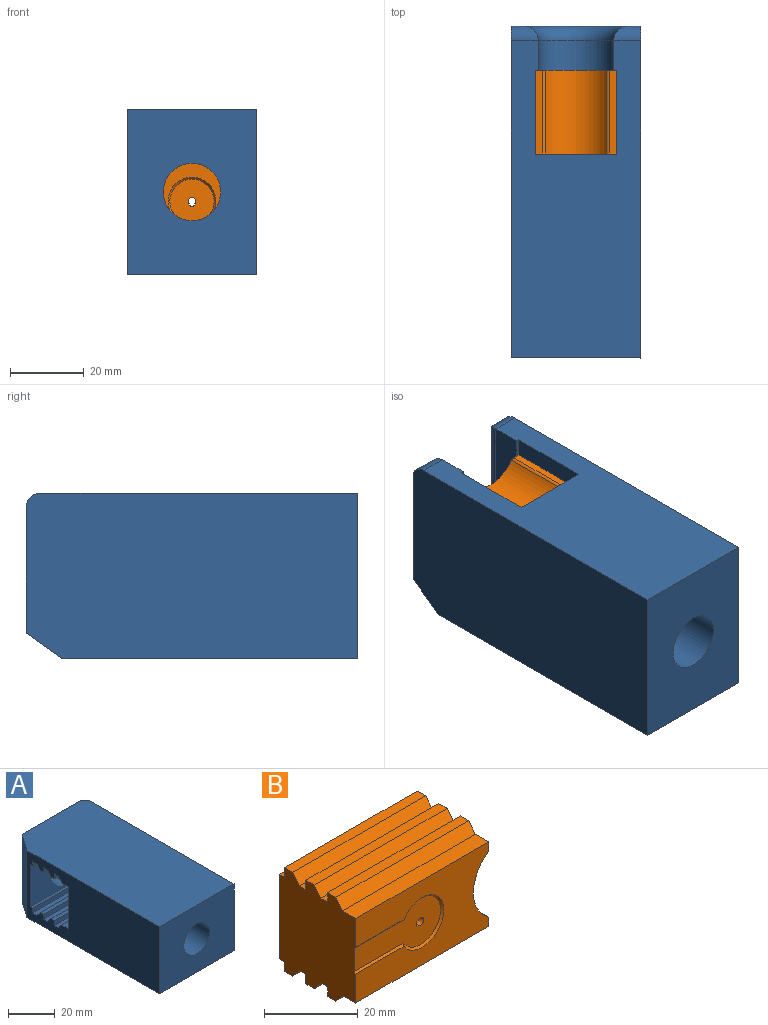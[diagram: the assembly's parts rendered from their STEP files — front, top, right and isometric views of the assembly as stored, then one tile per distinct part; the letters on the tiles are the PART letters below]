
ASSEMBLY  parts=2 mates=1
PART A: 50 faces, bbox 45x90x37 mm
  f0: plane 40x2.5mm, normal (0,-1,0), area 100mm2, adj f13,f27,f30,f46
  f1: plane 40x2.5mm, normal (0,0.78,-0.62), area 128.1mm2, adj f13,f27,f30,f46
  f2: plane 40x2.5mm, normal (0,-1,0), area 100mm2, adj f13,f27,f31,f45
  f3: plane 40x2.5mm, normal (0,0.78,-0.62), area 128.1mm2, adj f13,f27,f31,f45
  f4: plane 40x2.5mm, normal (0,-1,0), area 100mm2, adj f13,f27,f32,f44
  f5: plane 40x2.5mm, normal (0,0.78,-0.62), area 128.1mm2, adj f13,f27,f32,f44
  f6: plane 40x2.5mm, normal (0,0.78,0.62), area 128.1mm2, adj f13,f29,f33,f43
  f7: plane 40x2.5mm, normal (0,-1,0), area 100mm2, adj f13,f29,f33,f43
  f8: plane 40x2.5mm, normal (0,0.78,0.62), area 128.1mm2, adj f13,f29,f34,f42
  f9: plane 40x2.5mm, normal (0,-1,0), area 100mm2, adj f13,f29,f34,f42
  f10: plane 40x2.5mm, normal (0,0.78,0.62), area 128.1mm2, adj f13,f29,f35,f41
  f11: plane 40x2.5mm, normal (0,-1,0), area 100mm2, adj f13,f29,f35,f41
  f12: plane 86x35mm, normal (1,0,0), area 2340mm2, adj f15,f16,f17,f20,f25,f26,f27,f28
  f13: plane 80x35mm, normal (-1,0,0), area 2241.5mm2, adj f0,f1,f2,f3,f4,f5,f6,f7
  f14: plane 35x34mm, normal (0,1,0), area 343.8mm2, adj f15,f17,f36,f37,f38,f39,f40,f49
  f15: plane 90x45mm, normal (0,0,1), area 4011.6mm2, adj f12,f13,f14,f16,f36,f49
  f16: plane 45x35mm, normal (0,-1,0), area 1385.2mm2, adj f12,f13,f15,f17,f18
  f17: plane 90x45mm, normal (0,0,-1), area 4011.6mm2, adj f12,f13,f14,f16,f40,f49
  f18: cylinder r=7.77mm len=19.6mm, axis (0,-1,0), area 957.1mm2, adj f16,f24
  f19: cylinder r=10.25mm len=20.5mm, axis (0,-1,0), area 257.6mm2, adj f25,f26,f28,f38
  f20: plane 45x22mm, normal (0,1,0), area 691.4mm2, adj f12,f13,f21,f27,f29
  f21: cylinder r=9.75mm len=19.5mm, axis (0,-1,0), area 24.5mm2, adj f20,f22
  f22: plane 19.5x19.5mm, normal (0,1,0), area 44.2mm2, adj f21,f23
  f23: cylinder r=9mm len=25mm, axis (0,-1,0), area 1413.7mm2, adj f22,f24
  f24: cone r=7.77mm half-angle=7deg, axis (0,1,0), area 530.9mm2, adj f18,f23
  f25: plane 22.5x8mm, normal (0,0,1), area 180mm2, adj f12,f19,f28,f39
  f26: plane 22.5x8mm, normal (0,0,-1), area 180mm2, adj f12,f19,f28,f37
  f27: plane 45x23mm, normal (0,0,-1), area 495mm2, adj f0,f1,f2,f3,f4,f5,f12,f13
  f28: plane 45x22mm, normal (0,-1,0), area 363.7mm2, adj f12,f13,f19,f25,f26,f27,f29
  f29: plane 45x23mm, normal (0,0,1), area 495mm2, adj f6,f7,f8,f9,f10,f11,f12,f13
  f30: plane 40x2.5mm, normal (0,0,-1), area 100mm2, adj f0,f1,f13,f46
  f31: plane 40x2.5mm, normal (0,0,-1), area 100mm2, adj f2,f3,f13,f45
  f32: plane 40x2.5mm, normal (0,0,-1), area 100mm2, adj f4,f5,f13,f44
  f33: plane 40x2.5mm, normal (0,0,1), area 100mm2, adj f6,f7,f13,f43
  f34: plane 40x2.5mm, normal (0,0,1), area 100mm2, adj f8,f9,f13,f42
  f35: plane 40x2.5mm, normal (0,0,1), area 100mm2, adj f10,f11,f13,f41
  f36: cylinder r=4mm len=7.25mm, axis (0,0,-1), area 36.4mm2, adj f12,f14,f15,f37
  f37: cylinder r=4mm len=22.5mm, axis (-1,0,0), area 132.2mm2, adj f14,f26,f36,f38
  f38: torus R=14.25mm, axis (0,1,0), area 231mm2, adj f14,f19,f37,f39
  f39: cylinder r=4mm len=22.5mm, axis (1,0,0), area 132.2mm2, adj f14,f25,f38,f40
  f40: cylinder r=4mm len=7.25mm, axis (0,0,-1), area 36.4mm2, adj f12,f14,f17,f39
  f41: plane 4.5x2.5mm, normal (-1,0,0), area 8.8mm2, adj f10,f11,f29,f35
  f42: plane 4.5x2.5mm, normal (-1,0,0), area 8mm2, adj f8,f9,f29,f34,f47
  f43: plane 4.5x2.5mm, normal (-1,0,0), area 8.8mm2, adj f6,f7,f29,f33
  f44: plane 4.5x2.5mm, normal (-1,0,0), area 8.8mm2, adj f4,f5,f27,f32
  f45: plane 4.5x2.5mm, normal (-1,0,0), area 8.8mm2, adj f2,f3,f27,f31
  f46: plane 4.5x2.5mm, normal (-1,0,0), area 8.8mm2, adj f0,f1,f27,f30
  f47: cylinder r=0.5mm len=1mm, axis (-1,0,0), area 0mm2, adj f42,f48
  f48: plane 1x1mm, normal (-1,0,0), area 0.8mm2, adj f47
  f49: plane 35x10mm, normal (-0.82,0.57,0), area 427.2mm2, adj f13,f14,f15,f17
PART B: 55 faces, bbox 40x23x27 mm
  f0: plane 7x7mm, normal (0,1,0), area 34.8mm2, adj f41,f42,f43,f44,f45,f46,f47,f48
  f1: plane 23x4.42mm, normal (1,0,0), area 70.5mm2, adj f5,f6,f7,f8,f10,f11,f14,f15
  f2: plane 40x1.5mm, normal (0,0,-1), area 60mm2, adj f10,f12,f13,f31
  f3: plane 40x2mm, normal (0,0,-1), area 80mm2, adj f12,f13,f28,f29
  f4: plane 40x2mm, normal (0,0,-1), area 80mm2, adj f12,f13,f25,f26
  f5: plane 40x1.5mm, normal (0,0,1), area 60mm2, adj f1,f10,f13,f21
  f6: plane 40x2mm, normal (0,0,1), area 80mm2, adj f1,f13,f18,f20
  f7: plane 40x2mm, normal (0,0,1), area 80mm2, adj f1,f13,f15,f17
  f8: plane 40x22mm, normal (0,-1,0), area 594.9mm2, adj f1,f9,f11,f12,f13,f32,f33,f34
  f9: plane 40x4mm, normal (0,0,-1), area 160mm2, adj f8,f12,f13,f23
  f10: plane 40x22mm, normal (0,1,0), area 745.9mm2, adj f1,f2,f5,f12,f13,f32,f33,f34
  f11: plane 40x4mm, normal (0,0,1), area 160mm2, adj f1,f8,f13,f14
  f12: plane 23x4.42mm, normal (1,0,0), area 69.7mm2, adj f2,f3,f4,f8,f9,f10,f23,f24
  f13: plane 27x23mm, normal (-1,0,0), area 555.2mm2, adj f2,f3,f4,f5,f6,f7,f8,f9
  f14: plane 40x2.5mm, normal (0,-0.78,0.62), area 128.1mm2, adj f1,f11,f13,f16
  f15: plane 40x2.5mm, normal (0,1,0), area 100mm2, adj f1,f7,f13,f16
  f16: plane 40x2.5mm, normal (0,0,1), area 100mm2, adj f1,f13,f14,f15
  f17: plane 40x2.5mm, normal (0,-0.78,0.62), area 128.1mm2, adj f1,f7,f13,f19
  f18: plane 40x2.5mm, normal (0,1,0), area 100mm2, adj f1,f6,f13,f19
  f19: plane 40x2.5mm, normal (0,0,1), area 100mm2, adj f1,f13,f17,f18
  f20: plane 40x2.5mm, normal (0,-0.78,0.62), area 128.1mm2, adj f1,f6,f13,f22
  f21: plane 40x2.5mm, normal (0,1,0), area 100mm2, adj f1,f5,f13,f22
  f22: plane 40x2.5mm, normal (0,0,1), area 100mm2, adj f1,f13,f20,f21
  f23: plane 40x2.5mm, normal (0,-0.78,-0.62), area 128.1mm2, adj f9,f12,f13,f24
  f24: plane 40x2.5mm, normal (0,0,-1), area 100mm2, adj f12,f13,f23,f25
  f25: plane 40x2.5mm, normal (0,1,0), area 100mm2, adj f4,f12,f13,f24
  f26: plane 40x2.5mm, normal (0,-0.78,-0.62), area 128.1mm2, adj f4,f12,f13,f27
  f27: plane 40x2.5mm, normal (0,0,-1), area 100mm2, adj f12,f13,f26,f28
  f28: plane 40x2.5mm, normal (0,1,0), area 100mm2, adj f3,f12,f13,f27
  f29: plane 40x2.5mm, normal (0,-0.78,-0.62), area 128.1mm2, adj f3,f12,f13,f30
  f30: plane 40x2.5mm, normal (0,0,-1), area 100mm2, adj f12,f13,f29,f31
  f31: plane 40x2.5mm, normal (0,1,0), area 100mm2, adj f2,f12,f13,f30
  f32: cylinder r=10.25mm len=23mm, axis (0,1,0), area 442.7mm2, adj f8,f10,f33,f34
  f33: cylinder r=1mm len=23mm, axis (0,1,0), area 21.6mm2, adj f8,f10,f12,f32
  f34: cylinder r=1mm len=23mm, axis (0,1,0), area 21.6mm2, adj f1,f8,f10,f32
  f35: cylinder r=0.5mm len=1mm, axis (-1,0,0), area 0mm2, adj f12,f36
  f36: plane 1x1mm, normal (1,0,0), area 0.8mm2, adj f35
  f37: plane 26x12mm, normal (0,-1,0), area 195mm2, adj f13,f38,f39,f40,f42,f43,f44,f45
  f38: plane 14.81x0.51mm, normal (0,-0.71,-0.71), area 10.4mm2, adj f8,f13,f37,f39
  f39: cone r=6mm half-angle=45deg, axis (0,-1,0), area 22.9mm2, adj f8,f37,f38,f40
  f40: plane 14.81x0.51mm, normal (0,-0.71,0.71), area 10.4mm2, adj f8,f13,f37,f39
  f41: cylinder r=3.5mm len=18.5mm, axis (0,1,0), area 406.8mm2, adj f0,f54
  f42: cylinder r=1mm len=3.5mm, axis (0,-1,0), area 16.6mm2, adj f0,f37,f43,f51
  f43: plane 3.5x0.5mm, normal (0,0,-1), area 1.8mm2, adj f0,f37,f42,f44
  f44: plane 3.5x0.35mm, normal (1,0,0), area 1.2mm2, adj f0,f37,f43,f45
  f45: plane 3.5x0.1mm, normal (0,0,-1), area 0.4mm2, adj f0,f37,f44,f46
  f46: plane 3.5x0.15mm, normal (-1,0,0), area 0.5mm2, adj f0,f37,f45,f47
  f47: plane 3.5x0.05mm, normal (0,0,-1), area 0.2mm2, adj f0,f37,f46,f48
  f48: plane 3.5x1mm, normal (1,0,0), area 3.5mm2, adj f0,f37,f47,f49
  f49: plane 3.5x0.05mm, normal (0,0,1), area 0.2mm2, adj f0,f37,f48,f50
  f50: plane 3.5x0.15mm, normal (-1,0,0), area 0.5mm2, adj f0,f37,f49,f52
  f51: plane 3.5x0.5mm, normal (0,0,1), area 1.8mm2, adj f0,f37,f42,f53
  f52: plane 3.5x0.1mm, normal (0,0,1), area 0.4mm2, adj f0,f37,f50,f53
  f53: plane 3.5x0.35mm, normal (1,0,0), area 1.2mm2, adj f0,f37,f51,f52
  f54: cone r=3.5mm half-angle=71.6deg, axis (0,1,0), area 42.2mm2, adj f10,f41
PLACE A rot(axis=(0,-1,0),90deg) t=(51.13,-25.42,-38.23)mm fixed
PLACE B rot(axis=(0,-1,0),90deg) t=(51.13,-22.23,-40.73)mm
MATE slider A.f47 <-> B.f35  axis (0,0,-1) through (63.13,-13.79,-20.72)mm
